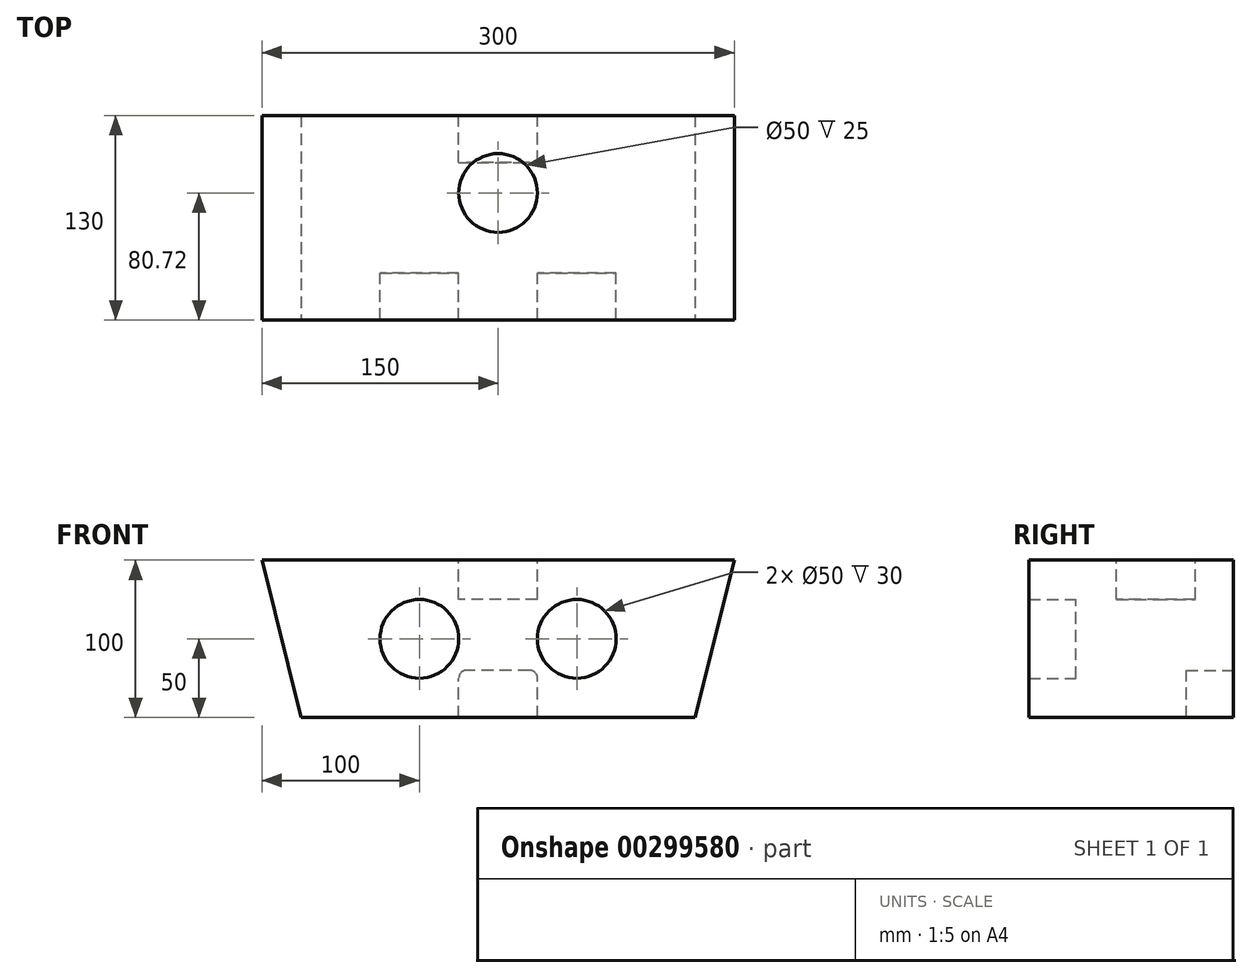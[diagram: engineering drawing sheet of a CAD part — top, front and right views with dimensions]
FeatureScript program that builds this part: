
annotation { "Feature Type Name" : "Feature", "Feature Type Description" : "" }
export const myFeature = defineFeature(function(context is Context, id is Id, definition is map)
    precondition{}
    {
        {
            var Q0;
            Q0=qCreatedBy(makeId("Front.planeOp"),FACE);
            var sketch = newSketch(context, id + "F0", { "sketchPlane" : qUnion([Q0])});
            skLineSegment(sketch, "E0.bottom", {"start": v(-125, 50) * mm, "end": v(125, 50) * mm});
            skLineSegment(sketch, "E0.top", {"start": v(-125, -50) * mm, "end": v(125, -50) * mm});
            skPoint(sketch, "E0.middle", {"position": v(0, 0) * mm});
            skLineSegment(sketch, "E1", {"start": v(-125, 50) * mm, "end": v(-150, 50) * mm});
            skLineSegment(sketch, "E2", {"start": v(125, 50) * mm, "end": v(150, 50) * mm});
            skLineSegment(sketch, "E3", {"start": v(125, -50) * mm, "end": v(150, 50) * mm});
            skLineSegment(sketch, "E4", {"start": v(-150, 50) * mm, "end": v(-125, -50) * mm});
            skSolve(sketch);
        }
        {
            var Q0;
            Q0=makeQuery(id+"F0.imprint","IMPRINT",FACE,{"disambiguationData":[TD([[makeQuery(id+"F0.imprint","IMPRINT",EDGE,{"derivedFrom":sQuery(id+"F0.wireOp",EDGE,"E0.bottom")}),-1.0]])]});
            extrude(context, id + "F1", {"entities" : qUnion([Q0]), "oppositeDirection" : true, "depth" : 100 * mm});
        }
        {
            var Q0;
            Q0=makeQuery(id+"F1.opExtrude","CAP_FACE",FACE,{"disambiguationData":[OSD([sQuery(id+"F0.wireOp",EDGE,"E0.bottom"),sQuery(id+"F0.wireOp",EDGE,"E0.top"),sQuery(id+"F0.wireOp",EDGE,"E1"),sQuery(id+"F0.wireOp",EDGE,"E2"),sQuery(id+"F0.wireOp",EDGE,"E3"),sQuery(id+"F0.wireOp",EDGE,"E4")])],"isStart":true});
            var sketch = newSketch(context, id + "F2", { "sketchPlane" : qUnion([Q0])});
            skLineSegment(sketch, "E5", {"start": v(0, 0) * mm, "end": v(25, 0) * mm});
            skLineSegment(sketch, "E6", {"start": v(25, 0) * mm, "end": v(0, 0) * mm});
            skCircle(sketch, "E7", {"center": v(-50, 0) * mm, "radius": 25 * mm});
            skCircle(sketch, "E8", {"center": v(50, 0) * mm, "radius": 25 * mm});
            skSolve(sketch);
        }
        {
            var Q0;
            Q0=makeQuery(id+"F2.imprint","IMPRINT",FACE,{"disambiguationData":[TD([[makeQuery(id+"F2.imprint","IMPRINT",EDGE,{"derivedFrom":sQuery(id+"F2.wireOp",EDGE,"E7")}),-1.0]])]});
            extrude(context, id + "F3", {"entities" : qUnion([Q0]), "operationType" : NewBodyOperationType.ADD, "depth" : 30 * mm});
        }
        {
            var Q0;
            {var subQ0=sQuery(id+"F0.wireOp",EDGE,"E2");var subQ1=sQuery(id+"F0.wireOp",EDGE,"E1");var subQ2=sQuery(id+"F0.wireOp",EDGE,"E0.bottom");Q0=makeQuery(id+"F3.boolean.opBoolean","MERGE",FACE,{"derivedFrom":[makeQuery(id+"F1.opExtrude","SWEPT_FACE",FACE,{"disambiguationData":[OSD([subQ2,subQ1,subQ0])]}),makeQuery(id+"F3.opExtrude","SWEPT_FACE",FACE,{"disambiguationData":[OSD([subQ2,subQ1,subQ0])]})]});}
            var sketch = newSketch(context, id + "F4", { "sketchPlane" : qUnion([Q0])});
            skCircle(sketch, "E9", {"center": v(0, 50.72) * mm, "radius": 25 * mm});
            skSolve(sketch);
        }
        {
            var Q0;
            Q0=makeQuery(id+"F4.imprint","IMPRINT",FACE,{"disambiguationData":[TD([[makeQuery(id+"F4.imprint","IMPRINT",EDGE,{"derivedFrom":sQuery(id+"F4.wireOp",EDGE,"E9")}),1.0]])]});
            extrude(context, id + "F5", {"entities" : qUnion([Q0]), "operationType" : NewBodyOperationType.REMOVE, "oppositeDirection" : true, "depth" : 25 * mm});
        }
        {
            var Q0;
            Q0=makeQuery(id+"F1.opExtrude","CAP_FACE",FACE,{"disambiguationData":[OSD([sQuery(id+"F0.wireOp",EDGE,"E0.bottom"),sQuery(id+"F0.wireOp",EDGE,"E0.top"),sQuery(id+"F0.wireOp",EDGE,"E1"),sQuery(id+"F0.wireOp",EDGE,"E2"),sQuery(id+"F0.wireOp",EDGE,"E3"),sQuery(id+"F0.wireOp",EDGE,"E4")])],"isStart":false});
            var sketch = newSketch(context, id + "F6", { "sketchPlane" : qUnion([Q0])});
            skLineSegment(sketch, "E10.bottom", {"start": v(0, -50) * mm, "end": v(-25, -50) * mm});
            skLineSegment(sketch, "E10.left", {"start": v(0, -50) * mm, "end": v(0, -50) * mm});
            skLineSegment(sketch, "E10.right", {"start": v(-25, -50) * mm, "end": v(-25, -50) * mm});
            skLineSegment(sketch, "E11.bottom", {"start": v(0, -50) * mm, "end": v(25, -50) * mm});
            skLineSegment(sketch, "E11.top", {"start": v(-20, -20) * mm, "end": v(20, -20) * mm});
            skLineSegment(sketch, "E11.left", {"start": v(-25, -50) * mm, "end": v(-25, -25) * mm});
            skLineSegment(sketch, "E11.right", {"start": v(25, -50) * mm, "end": v(25, -25) * mm});
            skPoint(sketch, "E12.start.orphan", {"position": v(0, -2.16) * mm});
            skPoint(sketch, "E13.visualSharp", {"position": v(-25, -20) * mm});
            skArc(sketch, "E13.filletArc", {"start": v(-20, -20) * mm, "mid": v(-23.54, -21.46) * mm, "end": v(-25, -25) * mm});
            skPoint(sketch, "E14.visualSharp", {"position": v(25, -20) * mm});
            skArc(sketch, "E14.filletArc", {"start": v(25, -25) * mm, "mid": v(23.54, -21.46) * mm, "end": v(20, -20) * mm});
            skSolve(sketch);
        }
        {
            var Q0;
            Q0=makeQuery(id+"F6.imprint","IMPRINT",FACE,{"disambiguationData":[TD([[makeQuery(id+"F6.imprint","IMPRINT",EDGE,{"derivedFrom":sQuery(id+"F6.wireOp",EDGE,"E10.bottom")}),-1.0]])]});
            extrude(context, id + "F7", {"entities" : qUnion([Q0]), "operationType" : NewBodyOperationType.REMOVE, "oppositeDirection" : true, "depth" : 30 * mm});
        }
    });
